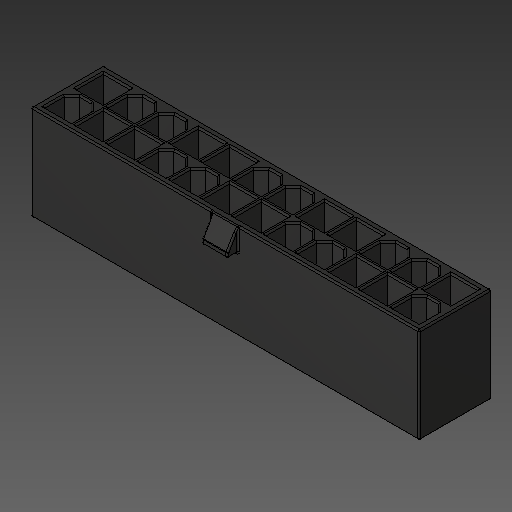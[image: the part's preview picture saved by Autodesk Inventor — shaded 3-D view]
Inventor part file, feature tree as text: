
AUTODESK INVENTOR PART (.ipt)
format: ipt  version: 2018.2 (Build 222227000, 227)  size: 320,000 bytes
history: native  units: mm
features: other x1, fillet x1
ambient origin geometry x8: Origin, YZ Plane, XZ Plane, XY Plane, X Axis, Y Axis, Z Axis, Center Point
bodies: Body1 (feature_tree)
feature tree (2):
  other  "ソリッド1"
  fillet  "Fillet1"  [1 undecoded]
note: 1 required parameter value undecoded (feature->parameter linkage not recoverable at this tier; creation-order binding heuristic only, values carry confidence <= 0.55)
